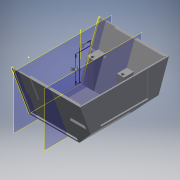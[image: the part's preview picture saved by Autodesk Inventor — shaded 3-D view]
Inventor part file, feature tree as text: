
AUTODESK INVENTOR PART (.ipt)
format: ipt  version: 2017 (Build 210142000, 142)  size: 278,016 bytes
history: native  units: mm
features: sketch x9, extrude x8, other x4, plane x4, reference x4, mirror x2, draft x1, fillet x1, chamfer x1, shell x1, projected_geometry x1
ambient origin geometry x8: Origin, YZ Plane, XZ Plane, XY Plane, X Axis, Y Axis, Z Axis, Center Point
bodies: Solid1 (feature_tree)
feature tree (36):
  extrude  "Extrusion1"  Depth=55.0mm
  draft  "FaceDraft1"
  fillet  "Fillet1"  Radius=31.0mm
  extrude  "Extrusion2"  Depth=78.0mm TaperAngle=0.0deg
  other  "Midplane"
  mirror  "Mirror1"
  extrude  "Extrusion3"  Depth=3.0mm
  extrude  "Extrusion5"  Depth=1.5mm TaperAngle=0.0deg
  extrude  "Extrusion6"  Depth=53.75mm
  chamfer  "Chamfer2"  Distance=53.75mm
  shell  "Shell1"  Thickness=1.75mm
  sketch  "Sketch7"  dims[d23=27.5mm]
  plane  "Work Plane5"
  extrude  "Extrusion7"  Depth=1.5mm TaperAngle=0.0deg
  extrude  "Extrusion8"  Depth=27.5mm
  mirror  "Mirror2"
  extrude  "Extrusion10"  Depth=53.75mm
  sketch  "Sketch1"  dims[d0=55.0mm d1=57.0mm d3=31.0mm]
  sketch  "Sketch2"  dims[d5=78.0mm d6=60.0mm d7=0.0mm]
  plane  "Work Plane1"
  plane  "Work Plane2"
  sketch  "Sketch3"  dims[d8=3.490659mm d9=3.0mm]
  sketch  "Sketch5"  dims[d10=1.5mm d13=1.5mm d14=0.0mm]
  sketch  "Sketch6"  dims[d17=1.5mm d18=0.0mm d22=53.75mm]
  plane  "Work Plane4"
  sketch  "Sketch9"  dims[d24=27.5mm]
  sketch  "Sketch10"  dims[d25=53.75mm]
  projected_geometry  "Projected Loop2"
  sketch  "Sketch12"  dims[d26=27.5mm d27=53.75mm d28=1.75mm d29=1.5mm d30=0.0mm d31=27.5mm d32=53.75mm d33=2.0mm d34=1.5mm d35=0.0mm d39=1.5mm d40=2.0mm d41=45.0deg d43=-8.25mm d44=-34.0mm d45=30.25mm d46=13.0mm d47=8.0mm d48=0.0mm d49=8.0mm d50=0.0mm d53=10.0mm d54=0.0mm]
  reference  "Reference8"
  reference  "Reference9"
  reference  "Reference10"
  reference  "Reference11"
  parser-record x1  (decoder bookkeeping rows leaked as tree rows — omitted from the tree; the rows remain in map.json)
  other  "Ganymede Node.iam"
  other  "core printed:1"
note: 1 file-system path scrubbed to <path> (originals preserved in map.json)
